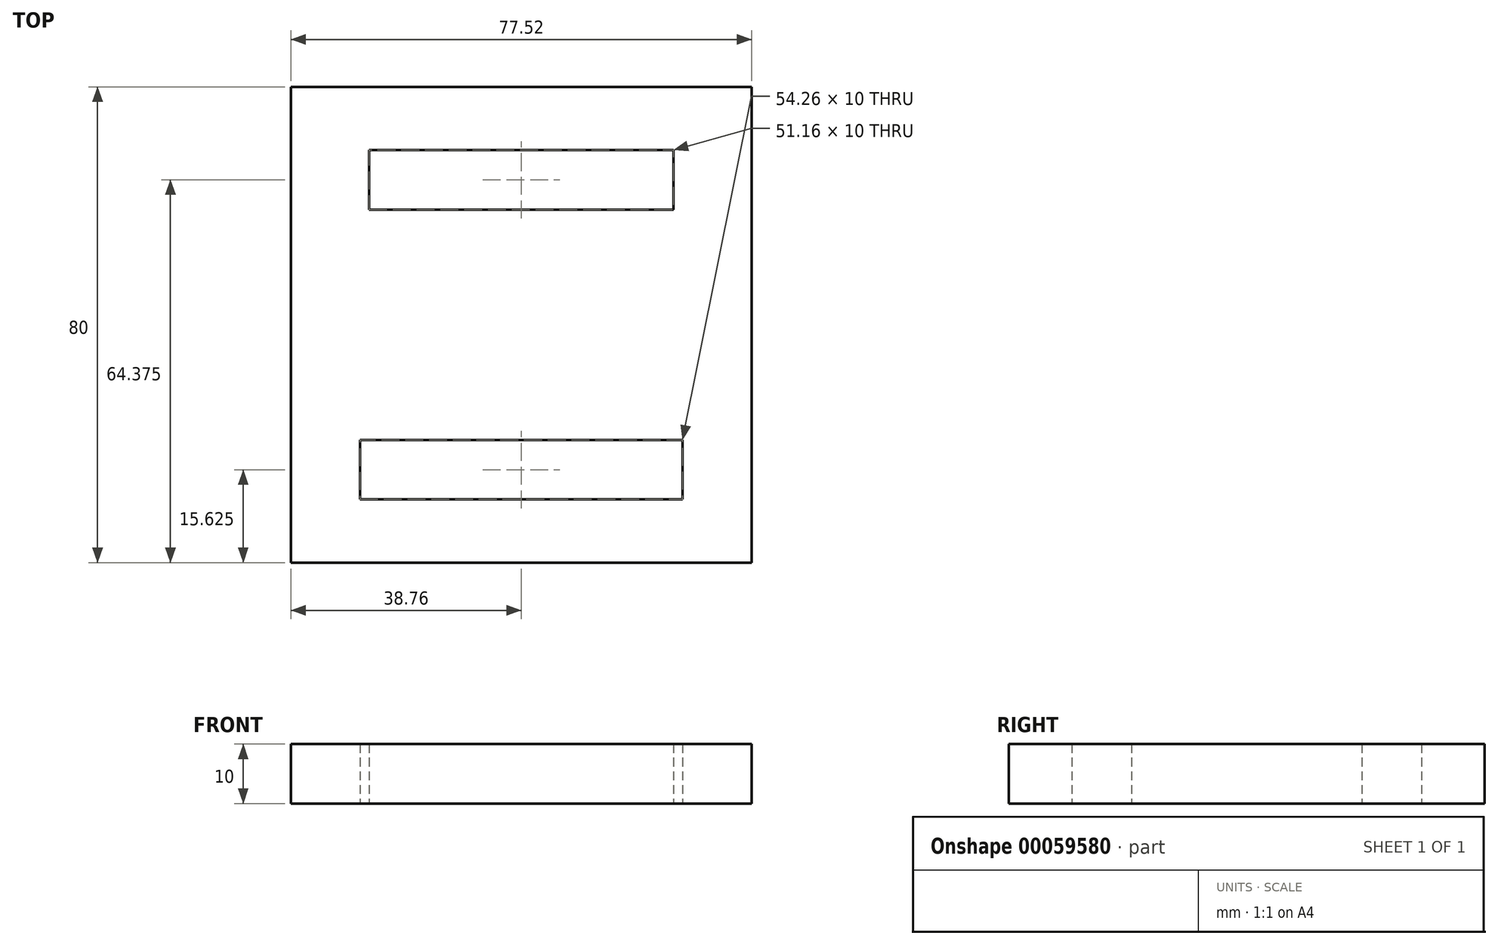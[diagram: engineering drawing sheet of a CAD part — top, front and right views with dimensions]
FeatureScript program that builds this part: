
annotation { "Feature Type Name" : "Feature", "Feature Type Description" : "" }
export const myFeature = defineFeature(function(context is Context, id is Id, definition is map)
    precondition{}
    {
        {
            var Q0;
            Q0=qCreatedBy(makeId("Top.planeOp"),FACE);
            var sketch = newSketch(context, id + "F0", { "sketchPlane" : qUnion([Q0])});
            skLineSegment(sketch, "E0.bottom", {"start": v(-38.76, 40) * mm, "end": v(38.76, 40) * mm});
            skLineSegment(sketch, "E0.top", {"start": v(-38.76, -40) * mm, "end": v(38.76, -40) * mm});
            skLineSegment(sketch, "E0.left", {"start": v(-38.76, 40) * mm, "end": v(-38.76, -40) * mm});
            skLineSegment(sketch, "E0.right", {"start": v(38.76, 40) * mm, "end": v(38.76, -40) * mm});
            skPoint(sketch, "E0.middle", {"position": v(0, 0) * mm});
            skLineSegment(sketch, "E1.bottom", {"start": v(-25.58, 29.38) * mm, "end": v(25.58, 29.38) * mm});
            skLineSegment(sketch, "E1.top", {"start": v(-25.58, 19.38) * mm, "end": v(25.58, 19.38) * mm});
            skLineSegment(sketch, "E1.left", {"start": v(-25.58, 29.38) * mm, "end": v(-25.58, 19.38) * mm});
            skLineSegment(sketch, "E1.right", {"start": v(25.58, 29.38) * mm, "end": v(25.58, 19.38) * mm});
            skPoint(sketch, "E1.middle", {"position": v(0, 24.38) * mm});
            skLineSegment(sketch, "E2.bottom", {"start": v(-27.13, -19.37) * mm, "end": v(27.13, -19.37) * mm});
            skLineSegment(sketch, "E2.top", {"start": v(-27.13, -29.38) * mm, "end": v(27.13, -29.38) * mm});
            skLineSegment(sketch, "E2.left", {"start": v(-27.13, -19.38) * mm, "end": v(-27.13, -29.38) * mm});
            skLineSegment(sketch, "E2.right", {"start": v(27.13, -19.38) * mm, "end": v(27.13, -29.38) * mm});
            skPoint(sketch, "E2.middle", {"position": v(0, -24.37) * mm});
            skSolve(sketch);
        }
        {
            var Q0;
            Q0 = qSketchRegion(id + "F0", true);
            extrude(context, id + "F1", {"entities" : qUnion([Q0]), "depth" : 10 * mm});
        }
    });
